# Revit family: Brutus_Chairs_BIM
name_source: partatom
category: Arredi
units: mm (PartAtom-declared; Revit-internal decimal feet)

## family parameters
Attiva taglio nelle viste = No
Basato su piano di lavoro = No
Condiviso = No
Numero OmniClass = 23.40.20.00
Origine composizione di rendering = Geometria famiglia
Punto di calcolo locali = No
Sempre verticale = Sì
Taglio con vuoti quando caricato = No
Titolo OmniClass = General Furniture and Specialties

## types (2) — shared parameters
AVAILABLE FINISHES = Ebonized black lacquer on Beech (EB). Raw effect lacquer on Oak (RE). Hand rubbed natural oil on Oak or Walnut (NA), or hand rubbed black oil on Walnut (BO).
BIM BADGE = https://bim.archiproducts.com
COLLECTION = BRUTUS
DEPTH = 534 mm
HEIGHT = 750 mm
MATERIAL DESCRIPTION = Carved solid wood. Seat in natural Vienna Cane or highly elastic woven membrane suspension with dense foam upholstery and welt detail.‎
PRODUCT SHEET = https://www.archiproducts.com
Produttore = BassamFellows
SEAT HEIGHT = 451 mm
STRUCTURE MATERIAL = BASSAM_FELLOWS_OAK_O-NA
TECHNICAL SHEET = https://bassamfellows.com
URL = https://bassamfellows.com
zero-valued in all types: Prospetto di default

## per-type parameters (varying)
| type | BASE MATERIAL | CB 47 VISIBILITY | CB 471 VISIBILITY | Descrizione | Modello | WIDTH |
| CB-47 | BASSAM_FELLOWS_CAPRI_17201_SNOW | Sì | No | Solid wood chair | Brutus Armless Chair | 576 mm |
| CB-471 | BASSAM_FELLOWS_COMFORT_LEATHER_02067_BEIGE | No | Sì | Solid wood chair with armrests | Brutus Armchair | 599 mm |

note: column(s) folded — value = type name in every type: PRODUCT CODE

## geometry (parser evidence)
native form markers: Sweep x1
no freeform markers — native parametric forms only
